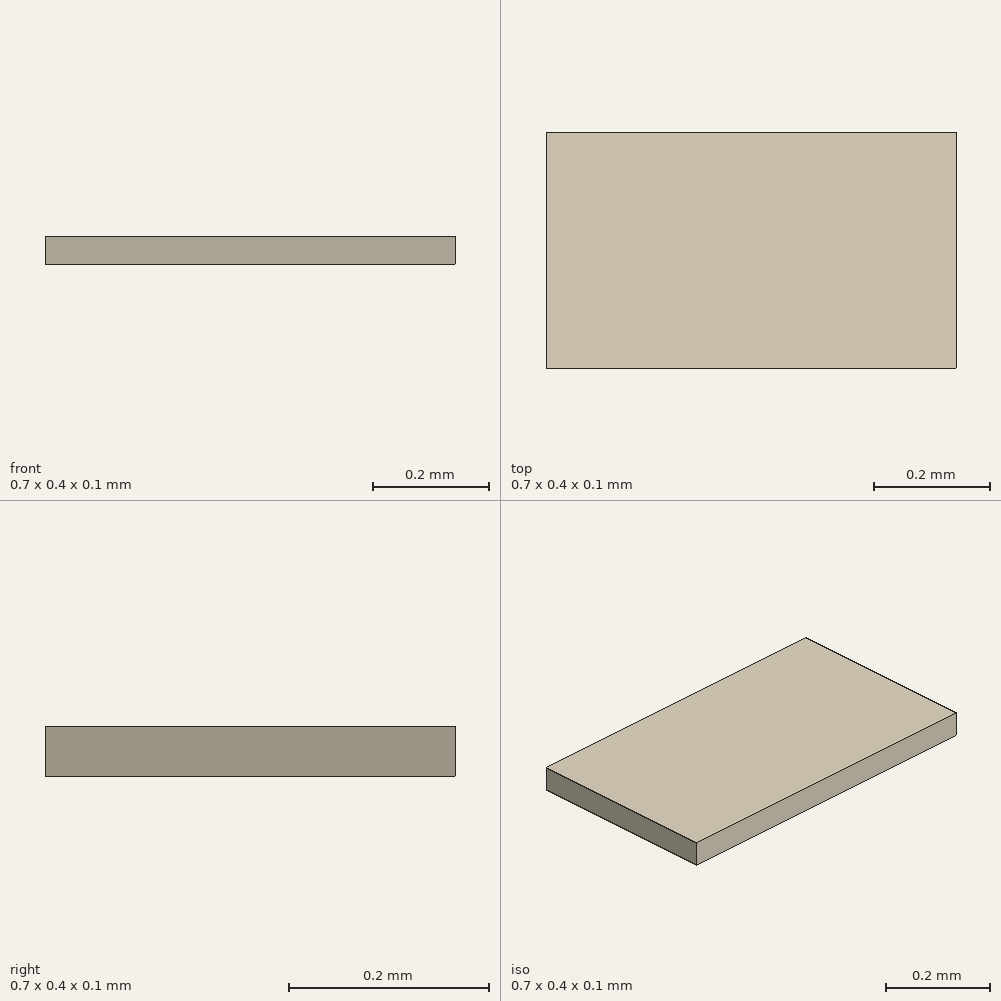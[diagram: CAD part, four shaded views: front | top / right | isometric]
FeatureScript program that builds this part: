
annotation { "Feature Type Name" : "Feature", "Feature Type Description" : "" }
export const myFeature = defineFeature(function(context is Context, id is Id, definition is map)
    precondition{}
    {
        {
            var Q0;
            Q0=qCreatedBy(makeId("Top.planeOp"),FACE);
            var sketch = newSketch(context, id + "F0", { "sketchPlane" : qUnion([Q0])});
            skLineSegment(sketch, "E0.bottom", {"start": v(-0.36, 0.2) * mm, "end": v(0.35, 0.2) * mm});
            skLineSegment(sketch, "E0.top", {"start": v(-0.36, -0.2) * mm, "end": v(0.35, -0.2) * mm});
            skLineSegment(sketch, "E0.left", {"start": v(-0.36, 0.2) * mm, "end": v(-0.36, -0.2) * mm});
            skLineSegment(sketch, "E0.right", {"start": v(0.35, 0.2) * mm, "end": v(0.35, -0.2) * mm});
            skLineSegment(sketch, "E1", {"start": v(-0.35, -0.2) * mm, "end": v(0.35, 0.2) * mm, "construction": true});
            skLineSegment(sketch, "E2", {"start": v(0.36, -0.2) * mm, "end": v(-0.36, 0.2) * mm, "construction": true});
            skPoint(sketch, "E3", {"position": v(0, 0) * mm});
            skSolve(sketch);
        }
        {
            var Q0;
            Q0 = qSketchRegion(id + "F0", true);
            extrude(context, id + "F1", {"entities" : qUnion([Q0]), "depth" : 0.05 * mm});
        }
    });
